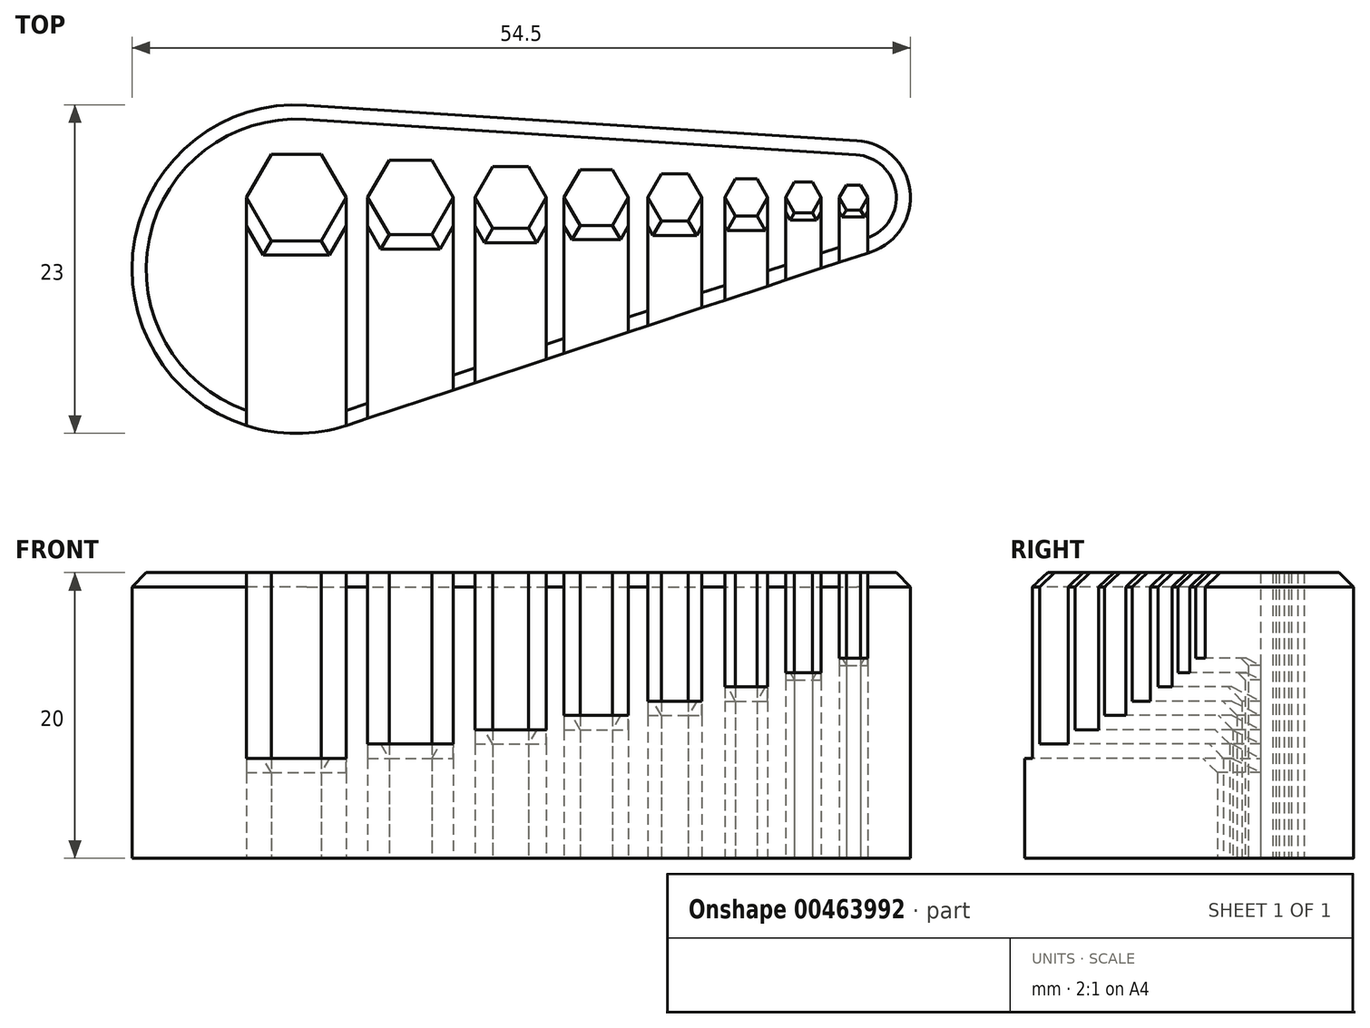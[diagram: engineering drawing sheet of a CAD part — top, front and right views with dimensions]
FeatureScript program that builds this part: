
annotation { "Feature Type Name" : "Feature", "Feature Type Description" : "" }
export const myFeature = defineFeature(function(context is Context, id is Id, definition is map)
    precondition{}
    {
        {
            var Q0;
            Q0=qCreatedBy(makeId("Top.planeOp"),FACE);
            var sketch = newSketch(context, id + "F0", { "sketchPlane" : qUnion([Q0])});
            skCircle(sketch, "E0.cCircle", {"center": v(0, 0) * mm, "radius": 2.25 * mm, "construction": true});
            skLineSegment(sketch, "E0.0", {"start": v(-1.12, 1.95) * mm, "end": v(1.12, 1.95) * mm});
            skLineSegment(sketch, "E0.1", {"start": v(1.12, 1.95) * mm, "end": v(2.25, 0) * mm});
            skLineSegment(sketch, "E0.2", {"start": v(2.25, 0) * mm, "end": v(1.12, -1.95) * mm});
            skLineSegment(sketch, "E0.3", {"start": v(1.12, -1.95) * mm, "end": v(-1.12, -1.95) * mm});
            skLineSegment(sketch, "E0.4", {"start": v(-1.12, -1.95) * mm, "end": v(-2.25, 0) * mm});
            skLineSegment(sketch, "E0.5", {"start": v(-2.25, 0) * mm, "end": v(-1.12, 1.95) * mm});
            skCircle(sketch, "E1.cCircle", {"center": v(5.5, 0) * mm, "radius": 1.9 * mm, "construction": true});
            skLineSegment(sketch, "E1.0", {"start": v(6.45, 1.65) * mm, "end": v(7.4, 0) * mm});
            skLineSegment(sketch, "E1.1", {"start": v(7.4, 0) * mm, "end": v(6.45, -1.65) * mm});
            skLineSegment(sketch, "E1.2", {"start": v(6.45, -1.65) * mm, "end": v(4.55, -1.65) * mm});
            skLineSegment(sketch, "E1.3", {"start": v(4.55, -1.65) * mm, "end": v(3.6, 0) * mm});
            skLineSegment(sketch, "E1.4", {"start": v(3.6, 0) * mm, "end": v(4.55, 1.65) * mm});
            skLineSegment(sketch, "E1.5", {"start": v(4.55, 1.65) * mm, "end": v(6.45, 1.65) * mm});
            skCircle(sketch, "E2.cCircle", {"center": v(10.5, 0) * mm, "radius": 1.5 * mm, "construction": true});
            skLineSegment(sketch, "E2.0", {"start": v(11.25, 1.3) * mm, "end": v(12, 0) * mm});
            skLineSegment(sketch, "E2.1", {"start": v(12, 0) * mm, "end": v(11.25, -1.3) * mm});
            skLineSegment(sketch, "E2.2", {"start": v(11.25, -1.3) * mm, "end": v(9.75, -1.3) * mm});
            skLineSegment(sketch, "E2.3", {"start": v(9.75, -1.3) * mm, "end": v(9, 0) * mm});
            skLineSegment(sketch, "E2.4", {"start": v(9, 0) * mm, "end": v(9.75, 1.3) * mm});
            skLineSegment(sketch, "E2.5", {"start": v(9.75, 1.3) * mm, "end": v(11.25, 1.3) * mm});
            skCircle(sketch, "E3.cCircle", {"center": v(-6, 0) * mm, "radius": 2.5 * mm, "construction": true});
            skLineSegment(sketch, "E3.0", {"start": v(-4.75, 2.17) * mm, "end": v(-3.5, 0) * mm});
            skLineSegment(sketch, "E3.1", {"start": v(-3.5, 0) * mm, "end": v(-4.75, -2.17) * mm});
            skLineSegment(sketch, "E3.2", {"start": v(-4.75, -2.17) * mm, "end": v(-7.25, -2.17) * mm});
            skLineSegment(sketch, "E3.3", {"start": v(-7.25, -2.17) * mm, "end": v(-8.5, 0) * mm});
            skLineSegment(sketch, "E3.4", {"start": v(-8.5, 0) * mm, "end": v(-7.25, 2.17) * mm});
            skLineSegment(sketch, "E3.5", {"start": v(-7.25, 2.17) * mm, "end": v(-4.75, 2.17) * mm});
            skCircle(sketch, "E4.cCircle", {"center": v(-13, 0) * mm, "radius": 3 * mm, "construction": true});
            skLineSegment(sketch, "E4.0", {"start": v(-11.5, 2.6) * mm, "end": v(-10, 0) * mm});
            skLineSegment(sketch, "E4.1", {"start": v(-10, 0) * mm, "end": v(-11.5, -2.6) * mm});
            skLineSegment(sketch, "E4.2", {"start": v(-11.5, -2.6) * mm, "end": v(-14.5, -2.6) * mm});
            skLineSegment(sketch, "E4.3", {"start": v(-14.5, -2.6) * mm, "end": v(-16, 0) * mm});
            skLineSegment(sketch, "E4.4", {"start": v(-16, 0) * mm, "end": v(-14.5, 2.6) * mm});
            skLineSegment(sketch, "E4.5", {"start": v(-14.5, 2.6) * mm, "end": v(-11.5, 2.6) * mm});
            skLineSegment(sketch, "E5.0", {"start": v(-17.5, 0) * mm, "end": v(-19.25, -3.03) * mm});
            skLineSegment(sketch, "E5.1", {"start": v(-19.25, -3.03) * mm, "end": v(-22.75, -3.03) * mm});
            skLineSegment(sketch, "E5.2", {"start": v(-22.75, -3.03) * mm, "end": v(-24.5, 0) * mm});
            skLineSegment(sketch, "E5.3", {"start": v(-24.5, 0) * mm, "end": v(-22.75, 3.03) * mm});
            skLineSegment(sketch, "E5.4", {"start": v(-22.75, 3.03) * mm, "end": v(-19.25, 3.03) * mm});
            skLineSegment(sketch, "E5.5", {"start": v(-19.25, 3.03) * mm, "end": v(-17.5, 0) * mm});
            skCircle(sketch, "E6.cCircle", {"center": v(14.5, 0) * mm, "radius": 1.25 * mm, "construction": true});
            skLineSegment(sketch, "E6.0", {"start": v(15.13, 1.08) * mm, "end": v(15.75, 0) * mm});
            skLineSegment(sketch, "E6.1", {"start": v(15.75, 0) * mm, "end": v(15.13, -1.08) * mm});
            skLineSegment(sketch, "E6.2", {"start": v(15.13, -1.08) * mm, "end": v(13.88, -1.08) * mm});
            skLineSegment(sketch, "E6.3", {"start": v(13.88, -1.08) * mm, "end": v(13.25, 0) * mm});
            skLineSegment(sketch, "E6.4", {"start": v(13.25, 0) * mm, "end": v(13.87, 1.08) * mm});
            skLineSegment(sketch, "E6.5", {"start": v(13.87, 1.08) * mm, "end": v(15.13, 1.08) * mm});
            skLineSegment(sketch, "E7.0", {"start": v(17.5, 0.87) * mm, "end": v(18.5, 0.87) * mm});
            skLineSegment(sketch, "E7.1", {"start": v(18.5, 0.87) * mm, "end": v(19, 0) * mm});
            skLineSegment(sketch, "E7.2", {"start": v(19, 0) * mm, "end": v(18.5, -0.87) * mm});
            skLineSegment(sketch, "E7.3", {"start": v(18.5, -0.87) * mm, "end": v(17.5, -0.87) * mm});
            skLineSegment(sketch, "E7.4", {"start": v(17.5, -0.87) * mm, "end": v(17, 0) * mm});
            skLineSegment(sketch, "E7.5", {"start": v(17, 0) * mm, "end": v(17.5, 0.87) * mm});
            skLineSegment(sketch, "E8", {"start": v(18.06, 1) * mm, "end": v(-20.78, 3.5) * mm, "construction": true});
            skLineSegment(sketch, "E9", {"start": v(18.06, -1) * mm, "end": v(18.06, -1) * mm});
            skArc(sketch, "E10", {"start": v(-22.86, 2.96) * mm, "mid": v(-24.33, -1.08) * mm, "end": v(-20.78, -3.5) * mm, "construction": true});
            skArc(sketch, "E11", {"start": v(-20.78, 3.5) * mm, "mid": v(-21.86, 3.4) * mm, "end": v(-22.86, 2.96) * mm, "construction": true});
            skArc(sketch, "E12", {"start": v(-20.78, -3.5) * mm, "mid": v(-17.5, 0) * mm, "end": v(-20.78, 3.5) * mm, "construction": true});
            skLineSegment(sketch, "E13", {"start": v(18.06, -1) * mm, "end": v(-20.78, -3.5) * mm, "construction": true});
            skArc(sketch, "E14", {"start": v(18.06, 1) * mm, "mid": v(17, 0) * mm, "end": v(18.06, -1) * mm, "construction": true});
            skArc(sketch, "E15", {"start": v(18.06, -1) * mm, "mid": v(19, 0) * mm, "end": v(18.06, 1) * mm, "construction": true});
            skLineSegment(sketch, "E16.0", {"start": v(18.26, 4) * mm, "end": v(-20.58, 6.49) * mm, "construction": true});
            skArc(sketch, "E16.1", {"start": v(18.26, -4) * mm, "mid": v(22, 0) * mm, "end": v(18.26, 4) * mm, "construction": true});
            skArc(sketch, "E16.2", {"start": v(-20.58, 6.49) * mm, "mid": v(-22.6, 6.3) * mm, "end": v(-24.45, 5.5) * mm, "construction": true});
            skArc(sketch, "E16.3", {"start": v(-24.45, 5.5) * mm, "mid": v(-27.19, -2) * mm, "end": v(-20.58, -6.49) * mm, "construction": true});
            skLineSegment(sketch, "E16.4", {"start": v(18.26, -4) * mm, "end": v(-20.58, -6.49) * mm, "construction": true});
            skLineSegment(sketch, "E17", {"start": v(-24.5, 0) * mm, "end": v(-24.5, -15.96) * mm});
            skLineSegment(sketch, "E18", {"start": v(-17.5, 0) * mm, "end": v(-17.5, -15.96) * mm});
            skLineSegment(sketch, "E19", {"start": v(-16, 0) * mm, "end": v(-16, -15.47) * mm});
            skLineSegment(sketch, "E20", {"start": v(-10, 0) * mm, "end": v(-10, -13.48) * mm});
            skLineSegment(sketch, "E21", {"start": v(-8.5, 0) * mm, "end": v(-8.5, -12.99) * mm});
            skLineSegment(sketch, "E22", {"start": v(-3.5, 0) * mm, "end": v(-3.5, -11.33) * mm});
            skLineSegment(sketch, "E23", {"start": v(-2.25, 0) * mm, "end": v(-2.25, -10.92) * mm});
            skLineSegment(sketch, "E24", {"start": v(2.25, 0) * mm, "end": v(2.25, -9.43) * mm});
            skLineSegment(sketch, "E25", {"start": v(3.6, 0) * mm, "end": v(3.6, -8.98) * mm});
            skLineSegment(sketch, "E26", {"start": v(7.4, 0) * mm, "end": v(7.4, -7.72) * mm});
            skLineSegment(sketch, "E27", {"start": v(9, 0) * mm, "end": v(9, -7.2) * mm});
            skLineSegment(sketch, "E28", {"start": v(12, 0) * mm, "end": v(12, -6.2) * mm});
            skLineSegment(sketch, "E29", {"start": v(13.25, 0) * mm, "end": v(13.25, -5.79) * mm});
            skLineSegment(sketch, "E30", {"start": v(15.75, 0) * mm, "end": v(15.75, -4.96) * mm});
            skLineSegment(sketch, "E31", {"start": v(17, 0) * mm, "end": v(17, -4.54) * mm});
            skLineSegment(sketch, "E32", {"start": v(19, 0) * mm, "end": v(19, -3.88) * mm});
            skLineSegment(sketch, "E33", {"start": v(-21, 0) * mm, "end": v(-21, 0) * mm});
            skPoint(sketch, "E33.endSnap0", {"position": v(-21, -3.03) * mm});
            skLineSegment(sketch, "E34", {"start": v(-21, 0) * mm, "end": v(-21, -16.96) * mm, "construction": true});
            skLineSegment(sketch, "E35", {"start": v(18.26, 4) * mm, "end": v(-31.4, 7.18) * mm});
            skCircle(sketch, "E36", {"center": v(-21, -5.01) * mm, "radius": 11.5 * mm});
            skCircle(sketch, "E37", {"center": v(18, 0) * mm, "radius": 4 * mm});
            skLineSegment(sketch, "E38", {"start": v(19.26, -3.8) * mm, "end": v(-17.39, -15.93) * mm});
            skSolve(sketch);
        }
        {
            var Q0;
            {var subQ4=sQuery(id+"F0.wireOp",EDGE,"E4.4");Q0=makeQuery(id+"F0.imprint","IMPRINT",FACE,{"disambiguationData":[TD([[makeQuery(id+"F0.imprint","IMPRINT",EDGE,{"derivedFrom":subQ4}),1.0]])]});}
            var Q1;
            Q1=makeQuery(id+"F0.imprint","IMPRINT",FACE,{"disambiguationData":[TD([[makeQuery(id+"F0.imprint","IMPRINT",EDGE,{"derivedFrom":sQuery(id+"F0.wireOp",EDGE,"E0.0")}),1.0]])]});
            var Q2;
            {var subQ10=sQuery(id+"F0.wireOp",EDGE,"E6.0");Q2=makeQuery(id+"F0.imprint","IMPRINT",FACE,{"disambiguationData":[TD([[makeQuery(id+"F0.imprint","IMPRINT",EDGE,{"derivedFrom":subQ10}),1.0]])]});}
            var Q3;
            {var subQ0=sQuery(id+"F0.wireOp",EDGE,"E36");var subQ1=sQuery(id+"F0.wireOp",EDGE,"E20");var subQ2=makeQuery(id+"F0.imprint","INTERSECT",VERTEX,{"disambiguationData":[OD(0.0)],"derivedFrom":[subQ1,subQ0]});Q3=makeQuery(id+"F0.imprint","IMPRINT",FACE,{"disambiguationData":[TD([[makeQuery(id+"F0.imprint","IMPRINT",EDGE,{"disambiguationData":[TD([[subQ2,-1.0]])],"derivedFrom":subQ1}),1.0]])]});}
            var Q4;
            {var subQ0=sQuery(id+"F0.wireOp",EDGE,"E38");var subQ1=sQuery(id+"F0.wireOp",EDGE,"E30");var subQ2=makeQuery(id+"F0.imprint","INTERSECT",VERTEX,{"derivedFrom":[subQ1,subQ0]});Q4=makeQuery(id+"F0.imprint","IMPRINT",FACE,{"disambiguationData":[TD([[makeQuery(id+"F0.imprint","IMPRINT",EDGE,{"disambiguationData":[TD([[subQ2,1.0]])],"derivedFrom":subQ1}),1.0]])]});}
            var Q5;
            {var subQ0=sQuery(id+"F0.wireOp",EDGE,"E38");var subQ1=sQuery(id+"F0.wireOp",EDGE,"E32");var subQ2=makeQuery(id+"F0.imprint","INTERSECT",VERTEX,{"derivedFrom":[subQ1,subQ0]});Q5=makeQuery(id+"F0.imprint","IMPRINT",FACE,{"disambiguationData":[TD([[makeQuery(id+"F0.imprint","IMPRINT",EDGE,{"disambiguationData":[TD([[subQ2,1.0]])],"derivedFrom":subQ1}),1.0]])]});}
            var Q6;
            {var subQ0=sQuery(id+"F0.wireOp",EDGE,"E38");var subQ1=sQuery(id+"F0.wireOp",EDGE,"E19");var subQ2=makeQuery(id+"F0.imprint","INTERSECT",VERTEX,{"derivedFrom":[subQ1,subQ0]});Q6=makeQuery(id+"F0.imprint","IMPRINT",FACE,{"disambiguationData":[TD([[makeQuery(id+"F0.imprint","IMPRINT",EDGE,{"disambiguationData":[TD([[subQ2,1.0]])],"derivedFrom":subQ1}),-1.0]])]});}
            extrude(context, id + "F1", {"entities" : qUnion([Q0, Q1, Q2, Q3, Q4, Q5, Q6]), "depth" : 20 * mm});
        }
        {
            var Q0;
            Q0=makeQuery(id+"F0.imprint","IMPRINT",FACE,{"disambiguationData":[TD([[makeQuery(id+"F0.imprint","IMPRINT",EDGE,{"derivedFrom":sQuery(id+"F0.wireOp",EDGE,"E7.2")}),1.0]])]});
            var Q1;
            {var subQ0=sQuery(id+"F0.wireOp",EDGE,"E38");var subQ1=sQuery(id+"F0.wireOp",EDGE,"E31");var subQ2=makeQuery(id+"F0.imprint","INTERSECT",VERTEX,{"derivedFrom":[subQ1,subQ0]});Q1=makeQuery(id+"F0.imprint","IMPRINT",FACE,{"disambiguationData":[TD([[makeQuery(id+"F0.imprint","IMPRINT",EDGE,{"disambiguationData":[TD([[subQ2,1.0]])],"derivedFrom":subQ1}),1.0]])]});}
            extrude(context, id + "F2", {"entities" : qUnion([Q0, Q1]), "operationType" : NewBodyOperationType.ADD, "depth" : 14 * mm});
        }
        {
            var Q0;
            {var subQ6=sQuery(id+"F0.wireOp",EDGE,"E6.3");Q0=makeQuery(id+"F0.imprint","IMPRINT",FACE,{"disambiguationData":[TD([[makeQuery(id+"F0.imprint","IMPRINT",EDGE,{"derivedFrom":subQ6}),1.0]])]});}
            var Q1;
            {var subQ0=sQuery(id+"F0.wireOp",EDGE,"E6.1");Q1=makeQuery(id+"F0.imprint","IMPRINT",FACE,{"disambiguationData":[TD([[makeQuery(id+"F0.imprint","IMPRINT",EDGE,{"derivedFrom":subQ0}),1.0]])]});}
            extrude(context, id + "F3", {"entities" : qUnion([Q0, Q1]), "operationType" : NewBodyOperationType.ADD, "depth" : 13 * mm});
        }
        {
            var Q0;
            Q0=makeQuery(id+"F0.imprint","IMPRINT",FACE,{"disambiguationData":[TD([[makeQuery(id+"F0.imprint","IMPRINT",EDGE,{"derivedFrom":sQuery(id+"F0.wireOp",EDGE,"E2.1")}),1.0]])]});
            extrude(context, id + "F4", {"entities" : qUnion([Q0]), "operationType" : NewBodyOperationType.ADD, "depth" : 12 * mm});
        }
        {
            var Q0;
            Q0=makeQuery(id+"F0.imprint","IMPRINT",FACE,{"disambiguationData":[TD([[makeQuery(id+"F0.imprint","IMPRINT",EDGE,{"derivedFrom":sQuery(id+"F0.wireOp",EDGE,"E1.1")}),1.0]])]});
            extrude(context, id + "F5", {"entities" : qUnion([Q0]), "operationType" : NewBodyOperationType.ADD, "depth" : 11 * mm});
        }
        {
            var Q0;
            Q0=makeQuery(id+"F0.imprint","IMPRINT",FACE,{"disambiguationData":[TD([[makeQuery(id+"F0.imprint","IMPRINT",EDGE,{"derivedFrom":sQuery(id+"F0.wireOp",EDGE,"E0.2")}),1.0]])]});
            extrude(context, id + "F6", {"entities" : qUnion([Q0]), "operationType" : NewBodyOperationType.ADD, "depth" : 10 * mm});
        }
        {
            var Q0;
            Q0=makeQuery(id+"F0.imprint","IMPRINT",FACE,{"disambiguationData":[TD([[makeQuery(id+"F0.imprint","IMPRINT",EDGE,{"derivedFrom":sQuery(id+"F0.wireOp",EDGE,"E3.1")}),1.0]])]});
            extrude(context, id + "F7", {"entities" : qUnion([Q0]), "operationType" : NewBodyOperationType.ADD, "depth" : 9 * mm});
        }
        {
            var Q0;
            {var subQ0=sQuery(id+"F0.wireOp",EDGE,"E38");var subQ1=sQuery(id+"F0.wireOp",EDGE,"E19");var subQ2=makeQuery(id+"F0.imprint","INTERSECT",VERTEX,{"derivedFrom":[subQ1,subQ0]});Q0=makeQuery(id+"F0.imprint","IMPRINT",FACE,{"disambiguationData":[TD([[makeQuery(id+"F0.imprint","IMPRINT",EDGE,{"disambiguationData":[TD([[subQ2,1.0]])],"derivedFrom":subQ1}),1.0]])]});}
            var Q1;
            {var subQ4=sQuery(id+"F0.wireOp",EDGE,"E4.2");Q1=makeQuery(id+"F0.imprint","IMPRINT",FACE,{"disambiguationData":[TD([[makeQuery(id+"F0.imprint","IMPRINT",EDGE,{"derivedFrom":subQ4}),1.0]])]});}
            var Q2;
            {var subQ1=sQuery(id+"F0.wireOp",EDGE,"E4.1");var subQ3=sQuery(id+"F0.wireOp",EDGE,"E36");var subQ4=makeQuery(id+"F0.imprint","INTERSECT",VERTEX,{"derivedFrom":[subQ1,subQ3]});Q2=makeQuery(id+"F0.imprint","IMPRINT",FACE,{"disambiguationData":[TD([[makeQuery(id+"F0.imprint","IMPRINT",EDGE,{"disambiguationData":[TD([[subQ4,1.0]])],"derivedFrom":subQ3}),-1.0]])]});}
            extrude(context, id + "F8", {"entities" : qUnion([Q0, Q1, Q2]), "operationType" : NewBodyOperationType.ADD, "depth" : 8 * mm});
        }
        {
            var Q0;
            Q0=makeQuery(id+"F0.imprint","IMPRINT",FACE,{"disambiguationData":[TD([[makeQuery(id+"F0.imprint","IMPRINT",EDGE,{"derivedFrom":sQuery(id+"F0.wireOp",EDGE,"E5.0")}),1.0]])]});
            extrude(context, id + "F9", {"entities" : qUnion([Q0]), "operationType" : NewBodyOperationType.ADD, "depth" : 7 * mm});
        }
        {
            var Q0;
            {var subQ0=sQuery(id+"F0.wireOp",EDGE,"E36");Q0=makeQuery(id+"F1.opExtrude","CAP_EDGE",EDGE,{"disambiguationData":[OSD([subQ0]),TDD([makeQuery(id+"F0.imprint","IMPRINT",EDGE,{"disambiguationData":[TD([[makeQuery(id+"F0.imprint","INTERSECT",VERTEX,{"derivedFrom":[sQuery(id+"F0.wireOp",EDGE,"E17"),subQ0]}),1.0]])],"derivedFrom":subQ0})])],"isStart":false});}
            var Q1;
            Q1=makeQuery(id+"F9.opExtrude","CAP_EDGE",EDGE,{"disambiguationData":[OSD([sQuery(id+"F0.wireOp",EDGE,"E5.1")])],"isStart":false});
            var Q2;
            Q2=makeQuery(id+"F9.opExtrude","CAP_EDGE",EDGE,{"disambiguationData":[OSD([sQuery(id+"F0.wireOp",EDGE,"E5.2")])],"isStart":false});
            var Q3;
            Q3=makeQuery(id+"F9.opExtrude","CAP_EDGE",EDGE,{"disambiguationData":[OSD([sQuery(id+"F0.wireOp",EDGE,"E5.0")])],"isStart":false});
            var Q4;
            Q4=makeQuery(id+"F8.opExtrude","CAP_EDGE",EDGE,{"disambiguationData":[OSD([sQuery(id+"F0.wireOp",EDGE,"E4.3")])],"isStart":false});
            var Q5;
            Q5=makeQuery(id+"F8.opExtrude","CAP_EDGE",EDGE,{"disambiguationData":[OSD([sQuery(id+"F0.wireOp",EDGE,"E4.2")])],"isStart":false});
            var Q6;
            Q6=makeQuery(id+"F8.opExtrude","CAP_EDGE",EDGE,{"disambiguationData":[OSD([sQuery(id+"F0.wireOp",EDGE,"E4.1")])],"isStart":false});
            var Q7;
            Q7=makeQuery(id+"F7.opExtrude","CAP_EDGE",EDGE,{"disambiguationData":[OSD([sQuery(id+"F0.wireOp",EDGE,"E3.3")])],"isStart":false});
            var Q8;
            Q8=makeQuery(id+"F7.opExtrude","CAP_EDGE",EDGE,{"disambiguationData":[OSD([sQuery(id+"F0.wireOp",EDGE,"E3.2")])],"isStart":false});
            var Q9;
            Q9=makeQuery(id+"F7.opExtrude","CAP_EDGE",EDGE,{"disambiguationData":[OSD([sQuery(id+"F0.wireOp",EDGE,"E3.1")])],"isStart":false});
            var Q10;
            Q10=makeQuery(id+"F6.opExtrude","CAP_EDGE",EDGE,{"disambiguationData":[OSD([sQuery(id+"F0.wireOp",EDGE,"E0.4")])],"isStart":false});
            var Q11;
            Q11=makeQuery(id+"F6.opExtrude","CAP_EDGE",EDGE,{"disambiguationData":[OSD([sQuery(id+"F0.wireOp",EDGE,"E0.3")])],"isStart":false});
            var Q12;
            Q12=makeQuery(id+"F6.opExtrude","CAP_EDGE",EDGE,{"disambiguationData":[OSD([sQuery(id+"F0.wireOp",EDGE,"E0.2")])],"isStart":false});
            var Q13;
            Q13=makeQuery(id+"F5.opExtrude","CAP_EDGE",EDGE,{"disambiguationData":[OSD([sQuery(id+"F0.wireOp",EDGE,"E1.3")])],"isStart":false});
            var Q14;
            Q14=makeQuery(id+"F5.opExtrude","CAP_EDGE",EDGE,{"disambiguationData":[OSD([sQuery(id+"F0.wireOp",EDGE,"E1.2")])],"isStart":false});
            var Q15;
            Q15=makeQuery(id+"F5.opExtrude","CAP_EDGE",EDGE,{"disambiguationData":[OSD([sQuery(id+"F0.wireOp",EDGE,"E1.1")])],"isStart":false});
            var Q16;
            Q16=makeQuery(id+"F4.opExtrude","CAP_EDGE",EDGE,{"disambiguationData":[OSD([sQuery(id+"F0.wireOp",EDGE,"E2.3")])],"isStart":false});
            var Q17;
            Q17=makeQuery(id+"F4.opExtrude","CAP_EDGE",EDGE,{"disambiguationData":[OSD([sQuery(id+"F0.wireOp",EDGE,"E2.2")])],"isStart":false});
            var Q18;
            Q18=makeQuery(id+"F4.opExtrude","CAP_EDGE",EDGE,{"disambiguationData":[OSD([sQuery(id+"F0.wireOp",EDGE,"E2.1")])],"isStart":false});
            var Q19;
            {var subQ0=sQuery(id+"F0.wireOp",EDGE,"E36");var subQ1=makeQuery(id+"F0.imprint","INTERSECT",VERTEX,{"derivedFrom":[subQ0,sQuery(id+"F0.wireOp",EDGE,"E38")]});Q19=makeQuery(id+"F1.opExtrude","CAP_EDGE",EDGE,{"disambiguationData":[OSD([subQ0]),TDD([makeQuery(id+"F0.imprint","IMPRINT",EDGE,{"disambiguationData":[TD([[makeQuery(id+"F0.imprint","INTERSECT",VERTEX,{"derivedFrom":[sQuery(id+"F0.wireOp",EDGE,"E18"),subQ0]}),-1.0]])],"derivedFrom":subQ0}),makeQuery(id+"F0.imprint","IMPRINT",EDGE,{"disambiguationData":[TD([[subQ1,-1.0]])],"derivedFrom":subQ0})])],"isStart":false});}
            var Q20;
            {var subQ0=sQuery(id+"F0.wireOp",EDGE,"E38");Q20=makeQuery(id+"F1.opExtrude","CAP_EDGE",EDGE,{"disambiguationData":[OSD([subQ0]),TDD([makeQuery(id+"F0.imprint","IMPRINT",EDGE,{"disambiguationData":[TD([[makeQuery(id+"F0.imprint","INTERSECT",VERTEX,{"derivedFrom":[sQuery(id+"F0.wireOp",EDGE,"E20"),subQ0]}),1.0]])],"derivedFrom":subQ0})])],"isStart":false});}
            var Q21;
            {var subQ0=sQuery(id+"F0.wireOp",EDGE,"E38");Q21=makeQuery(id+"F1.opExtrude","CAP_EDGE",EDGE,{"disambiguationData":[OSD([subQ0]),TDD([makeQuery(id+"F0.imprint","IMPRINT",EDGE,{"disambiguationData":[TD([[makeQuery(id+"F0.imprint","INTERSECT",VERTEX,{"derivedFrom":[sQuery(id+"F0.wireOp",EDGE,"E22"),subQ0]}),1.0]])],"derivedFrom":subQ0})])],"isStart":false});}
            var Q22;
            {var subQ0=sQuery(id+"F0.wireOp",EDGE,"E38");Q22=makeQuery(id+"F1.opExtrude","CAP_EDGE",EDGE,{"disambiguationData":[OSD([subQ0]),TDD([makeQuery(id+"F0.imprint","IMPRINT",EDGE,{"disambiguationData":[TD([[makeQuery(id+"F0.imprint","INTERSECT",VERTEX,{"derivedFrom":[sQuery(id+"F0.wireOp",EDGE,"E24"),subQ0]}),1.0]])],"derivedFrom":subQ0})])],"isStart":false});}
            var Q23;
            {var subQ0=sQuery(id+"F0.wireOp",EDGE,"E38");Q23=makeQuery(id+"F1.opExtrude","CAP_EDGE",EDGE,{"disambiguationData":[OSD([subQ0]),TDD([makeQuery(id+"F0.imprint","IMPRINT",EDGE,{"disambiguationData":[TD([[makeQuery(id+"F0.imprint","INTERSECT",VERTEX,{"derivedFrom":[sQuery(id+"F0.wireOp",EDGE,"E26"),subQ0]}),1.0]])],"derivedFrom":subQ0})])],"isStart":false});}
            var Q24;
            {var subQ0=sQuery(id+"F0.wireOp",EDGE,"E38");Q24=makeQuery(id+"F1.opExtrude","CAP_EDGE",EDGE,{"disambiguationData":[OSD([subQ0]),TDD([makeQuery(id+"F0.imprint","IMPRINT",EDGE,{"disambiguationData":[TD([[makeQuery(id+"F0.imprint","INTERSECT",VERTEX,{"derivedFrom":[sQuery(id+"F0.wireOp",EDGE,"E28"),subQ0]}),1.0]])],"derivedFrom":subQ0})])],"isStart":false});}
            var Q25;
            {var subQ0=sQuery(id+"F0.wireOp",EDGE,"E38");Q25=makeQuery(id+"F1.opExtrude","CAP_EDGE",EDGE,{"disambiguationData":[OSD([subQ0]),TDD([makeQuery(id+"F0.imprint","IMPRINT",EDGE,{"disambiguationData":[TD([[makeQuery(id+"F0.imprint","INTERSECT",VERTEX,{"derivedFrom":[sQuery(id+"F0.wireOp",EDGE,"E30"),subQ0]}),1.0]])],"derivedFrom":subQ0})])],"isStart":false});}
            chamfer(context, id + "F10", {"entities" : qUnion([Q0, Q1, Q2, Q3, Q4, Q5, Q6, Q7, Q8, Q9, Q10, Q11, Q12, Q13, Q14, Q15, Q16, Q17, Q18, Q19, Q20, Q21, Q22, Q23, Q24, Q25]), "width" : 1 * mm, "tangentPropagation" : true});
        }
        {
            var Q0;
            Q0=makeQuery(id+"F3.opExtrude","CAP_EDGE",EDGE,{"disambiguationData":[OSD([sQuery(id+"F0.wireOp",EDGE,"E6.3")])],"isStart":false});
            var Q1;
            Q1=makeQuery(id+"F3.opExtrude","CAP_EDGE",EDGE,{"disambiguationData":[OSD([sQuery(id+"F0.wireOp",EDGE,"E6.2")])],"isStart":false});
            var Q2;
            Q2=makeQuery(id+"F3.opExtrude","CAP_EDGE",EDGE,{"disambiguationData":[OSD([sQuery(id+"F0.wireOp",EDGE,"E6.1")])],"isStart":false});
            var Q3;
            Q3=makeQuery(id+"F2.opExtrude","CAP_EDGE",EDGE,{"disambiguationData":[OSD([sQuery(id+"F0.wireOp",EDGE,"E7.4")])],"isStart":false});
            var Q4;
            Q4=makeQuery(id+"F2.opExtrude","CAP_EDGE",EDGE,{"disambiguationData":[OSD([sQuery(id+"F0.wireOp",EDGE,"E7.3")])],"isStart":false});
            var Q5;
            Q5=makeQuery(id+"F2.opExtrude","CAP_EDGE",EDGE,{"disambiguationData":[OSD([sQuery(id+"F0.wireOp",EDGE,"E7.2")])],"isStart":false});
            chamfer(context, id + "F11", {"entities" : qUnion([Q0, Q1, Q2, Q3, Q4, Q5]), "width" : 0.5 * mm, "tangentPropagation" : true});
        }
    });
